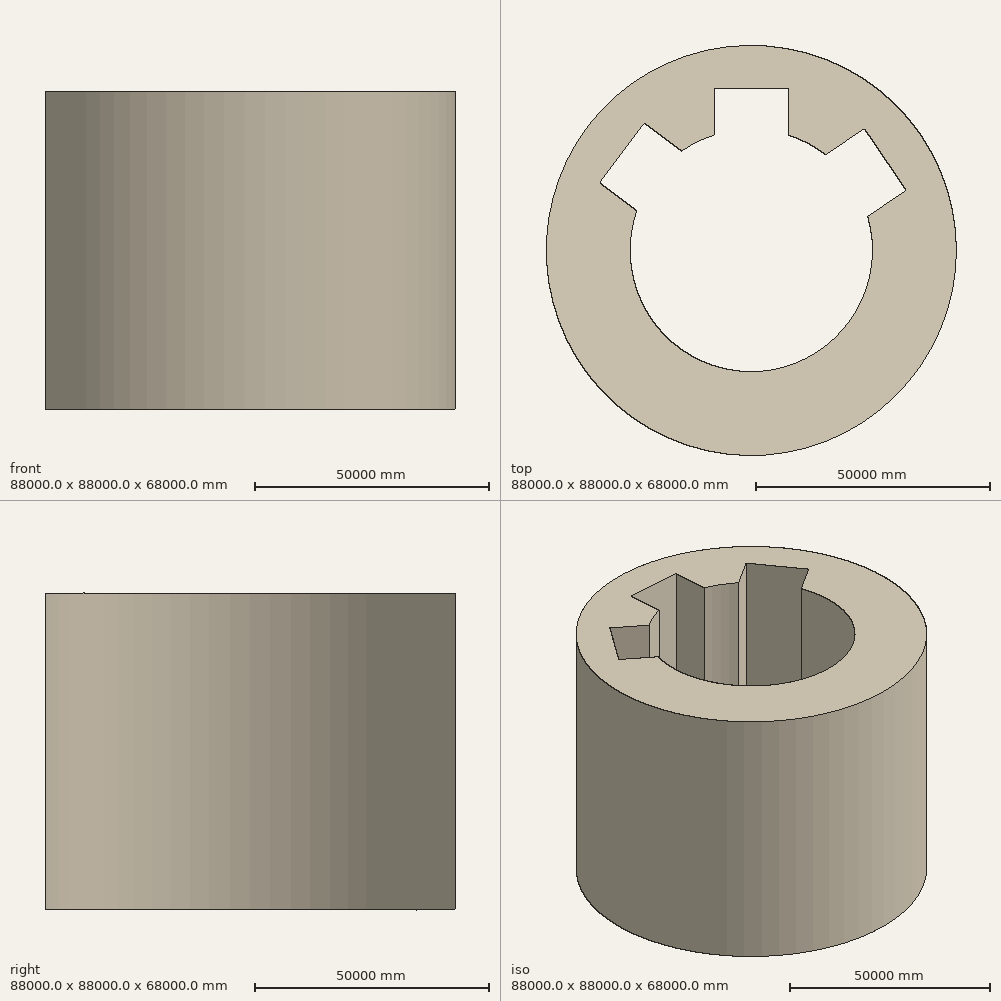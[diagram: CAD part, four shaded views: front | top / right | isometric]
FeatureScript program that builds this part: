
annotation { "Feature Type Name" : "Feature", "Feature Type Description" : "" }
export const myFeature = defineFeature(function(context is Context, id is Id, definition is map)
    precondition{}
    {
        {
            var Q0;
            Q0=qCreatedBy(makeId("Top.planeOp"),FACE);
            var sketch = newSketch(context, id + "F0", { "sketchPlane" : qUnion([Q0])});
            skCircle(sketch, "E0", {"center": v(0, 0) * mm, "radius": 44000 * mm});
            skCircle(sketch, "E1", {"center": v(0, 0) * mm, "radius": 26000 * mm});
            skLineSegment(sketch, "E2", {"start": v(-8000, 24738.63) * mm, "end": v(-8000, 34738.63) * mm});
            skLineSegment(sketch, "E3", {"start": v(-8000, 34738.63) * mm, "end": v(8000, 34738.63) * mm});
            skLineSegment(sketch, "E4", {"start": v(8000, 34738.63) * mm, "end": v(8000, 24738.63) * mm});
            skLineSegment(sketch, "E5", {"start": v(0, 0) * mm, "end": v(0, 39870.5) * mm});
            skLineSegment(sketch, "E6", {"start": v(15993.37, 20499.08) * mm, "end": v(24272.17, 26108.13) * mm});
            skLineSegment(sketch, "E7", {"start": v(24272.17, 26108.13) * mm, "end": v(33246.66, 12862.06) * mm});
            skLineSegment(sketch, "E8", {"start": v(33246.66, 12862.06) * mm, "end": v(24967.86, 7253) * mm});
            skLineSegment(sketch, "E9", {"start": v(-14930.28, 21285.83) * mm, "end": v(-22913.14, 27308.62) * mm});
            skLineSegment(sketch, "E10", {"start": v(-22913.14, 27308.62) * mm, "end": v(-32549.6, 14536.04) * mm});
            skLineSegment(sketch, "E11", {"start": v(-32549.6, 14536.04) * mm, "end": v(-24566.73, 8513.26) * mm});
            skSolve(sketch);
        }
        {
            var Q0;
            Q0 = qSketchRegion(id + "F0", true);
            extrude(context, id + "F1", {"entities" : qUnion([Q0]), "oppositeDirection" : true, "depth" : 68000 * mm, "offsetDistance" : 25 * mm});
        }
    });
